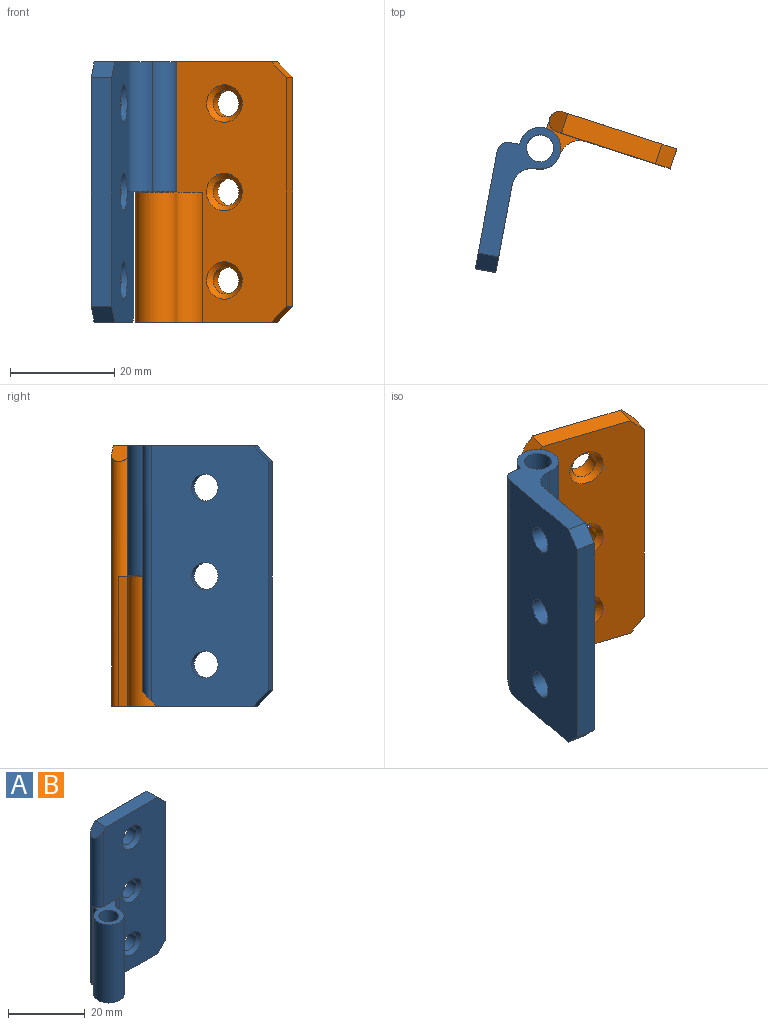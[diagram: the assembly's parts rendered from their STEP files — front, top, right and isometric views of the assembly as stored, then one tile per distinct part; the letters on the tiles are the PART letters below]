
ASSEMBLY  parts=2 mates=1
PART A: 20 faces, bbox 29x12x50 mm
  f0: plane 50x23mm, normal (0,-1,0), area 868.4mm2, adj f2,f3,f7,f11,f12,f13,f14,f15
  f1: plane 25x2mm, normal (-1,0,0), area 50mm2, adj f2,f9,f11,f16
  f2: plane 26x12mm, normal (0,0,-1), area 123mm2, adj f0,f1,f8,f9,f10,f12,f15,f16
  f3: plane 44x4mm, normal (1,0,0), area 176mm2, adj f0,f8,f14,f15
  f4: cylinder r=2.6mm len=5.2mm, axis (0,1,0), area 49mm2, adj f8,f19
  f5: cylinder r=2.6mm len=5.2mm, axis (0,1,0), area 49mm2, adj f8,f18
  f6: cylinder r=2.6mm len=5.2mm, axis (0,1,0), area 49mm2, adj f8,f17
  f7: plane 19x4mm, normal (0,0,1), area 76mm2, adj f0,f8,f13,f14
  f8: plane 50x23mm, normal (0,1,0), area 1076.8mm2, adj f2,f3,f4,f5,f6,f7,f13,f14
  f9: cylinder r=4mm len=25mm, axis (0,0,-1), area 471.2mm2, adj f1,f2,f11,f12
  f10: cylinder r=2.6mm len=25mm, axis (0,0,-1), area 408.4mm2, adj f2,f11
  f11: plane 12x10mm, normal (0,0,1), area 36.8mm2, adj f0,f1,f9,f10,f12,f16
  f12: cylinder r=4mm len=25mm, axis (0,0,-1), area 157.1mm2, adj f0,f2,f9,f11
  f13: plane 4x3mm, normal (-0.71,0,0.71), area 14.5mm2, adj f0,f7,f8,f16
  f14: plane 4x3mm, normal (0.71,0,0.71), area 17mm2, adj f0,f3,f7,f8
  f15: plane 4x3mm, normal (0.71,0,-0.71), area 17mm2, adj f0,f2,f3,f8
  f16: cylinder r=2mm len=49mm, axis (0,0,-1), area 221.3mm2, adj f0,f1,f2,f8,f11,f13
  f17: cone r=2.6mm half-angle=45deg, axis (0,-1,0), area 27.5mm2, adj f0,f6
  f18: cone r=2.6mm half-angle=45deg, axis (0,-1,0), area 27.5mm2, adj f0,f5
  f19: cone r=2.6mm half-angle=45deg, axis (0,-1,0), area 27.5mm2, adj f0,f4
PART B: same geometry as A
PLACE A rot(axis=(-0.64,0.77,0),180deg) t=(178.78,1.87,-184.24)mm
PLACE B rot(axis=(0,0,-1),18deg) t=(189.12,8.01,-134.24)mm
MATE revolute A.f9 <-> B.f9  axis (0,0,-1) through (186.65,0.41,-159.24)mm
